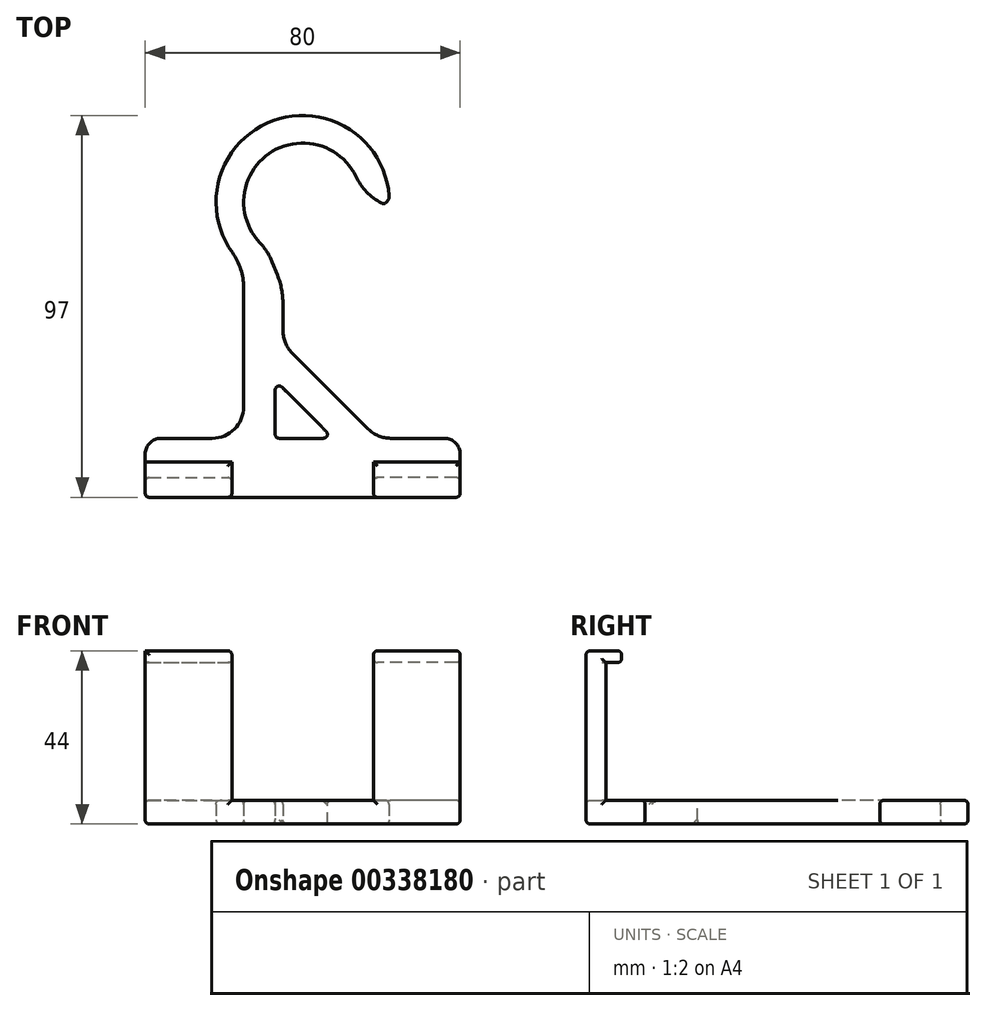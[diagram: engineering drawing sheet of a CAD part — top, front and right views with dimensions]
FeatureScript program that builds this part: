
annotation { "Feature Type Name" : "Feature", "Feature Type Description" : "" }
export const myFeature = defineFeature(function(context is Context, id is Id, definition is map)
    precondition{}
    {
        {
            var Q0;
            Q0=qCreatedBy(makeId("Top.planeOp"),FACE);
            var sketch = newSketch(context, id + "F0", { "sketchPlane" : qUnion([Q0])});
            skArc(sketch, "E0", {"start": v(13.52, 6.5) * mm, "mid": v(-8.54, 12.33) * mm, "end": v(-10.83, -10.37) * mm});
            skLineSegment(sketch, "E1.left", {"start": v(-15, -21.66) * mm, "end": v(-15, -52) * mm});
            skLineSegment(sketch, "E2", {"start": v(-23, -60) * mm, "end": v(-36, -60) * mm});
            skLineSegment(sketch, "E3", {"start": v(-40, -64) * mm, "end": v(-40, -75) * mm});
            skLineSegment(sketch, "E4", {"start": v(-40, -75) * mm, "end": v(40, -75) * mm});
            skLineSegment(sketch, "E5", {"start": v(40, -75) * mm, "end": v(40, -64) * mm});
            skLineSegment(sketch, "E6", {"start": v(36, -60) * mm, "end": v(22.31, -60) * mm});
            skLineSegment(sketch, "E7", {"start": v(-5, -25.91) * mm, "end": v(-5, -32.69) * mm});
            skLineSegment(sketch, "E8", {"start": v(-2.66, -38.34) * mm, "end": v(16.66, -57.66) * mm});
            skArc(sketch, "E9", {"start": v(21.94, 1.6) * mm, "mid": v(-7.53, 20.67) * mm, "end": v(-17.84, -12.88) * mm});
            skLineSegment(sketch, "E10", {"start": v(-7.72, -15.22) * mm, "end": v(-6.4, -18.54) * mm});
            skPoint(sketch, "E1.bottom.start.orphan", {"position": v(-15, 0) * mm});
            skLineSegment(sketch, "E11", {"start": v(-7, -45.31) * mm, "end": v(-7, -60) * mm});
            skLineSegment(sketch, "E12", {"start": v(-7, -60) * mm, "end": v(7.69, -60) * mm});
            skLineSegment(sketch, "E13", {"start": v(7.69, -60) * mm, "end": v(-7, -45.31) * mm});
            skPoint(sketch, "E14.visualSharp", {"position": v(-15, -16.1) * mm});
            skArc(sketch, "E14.filletArc", {"start": v(-15, -21.66) * mm, "mid": v(-15.73, -17.04) * mm, "end": v(-17.84, -12.88) * mm});
            skPoint(sketch, "E15.visualSharp", {"position": v(-5, -22.1) * mm});
            skArc(sketch, "E15.filletArc", {"start": v(-5, -25.91) * mm, "mid": v(-5.35, -22.16) * mm, "end": v(-6.4, -18.54) * mm});
            skPoint(sketch, "E16.visualSharp", {"position": v(-9, -12) * mm});
            skArc(sketch, "E16.filletArc", {"start": v(-7.72, -15.22) * mm, "mid": v(-9.04, -12.65) * mm, "end": v(-10.83, -10.37) * mm});
            skPoint(sketch, "E17.visualSharp", {"position": v(-5, -36) * mm});
            skArc(sketch, "E17.filletArc", {"start": v(-5, -32.69) * mm, "mid": v(-4.4, -35.75) * mm, "end": v(-2.66, -38.34) * mm});
            skPoint(sketch, "E18.visualSharp", {"position": v(19, -60) * mm});
            skArc(sketch, "E18.filletArc", {"start": v(16.66, -57.66) * mm, "mid": v(19.25, -59.4) * mm, "end": v(22.31, -60) * mm});
            skPoint(sketch, "E19.visualSharp", {"position": v(-15, -60) * mm});
            skArc(sketch, "E19.filletArc", {"start": v(-23, -60) * mm, "mid": v(-17.34, -57.66) * mm, "end": v(-15, -52) * mm});
            skPoint(sketch, "E20.visualSharp", {"position": v(40, -60) * mm});
            skArc(sketch, "E20.filletArc", {"start": v(40, -64) * mm, "mid": v(38.83, -61.17) * mm, "end": v(36, -60) * mm});
            skPoint(sketch, "E21.visualSharp", {"position": v(-40, -60) * mm});
            skArc(sketch, "E21.filletArc", {"start": v(-36, -60) * mm, "mid": v(-38.83, -61.17) * mm, "end": v(-40, -64) * mm});
            skPoint(sketch, "E22.visualSharp", {"position": v(22, 0) * mm});
            skArc(sketch, "E22.filletArc", {"start": v(18, 1) * mm, "mid": v(20.25, -0.52) * mm, "end": v(21.94, 1.6) * mm});
            skPoint(sketch, "E23.visualSharp", {"position": v(14.7, 3) * mm});
            skArc(sketch, "E23.filletArc", {"start": v(13.52, 6.5) * mm, "mid": v(16.4, 2.43) * mm, "end": v(20.45, -0.48) * mm});
            skSolve(sketch);
        }
        {
            var Q0;
            Q0 = qSketchRegion(id + "F0", true);
            extrude(context, id + "F1", {"entities" : qUnion([Q0]), "depth" : 6 * mm});
        }
        {
            var Q0;
            Q0=makeQuery(id+"F1.opExtrude","CAP_FACE",FACE,{"disambiguationData":[OSD([sQuery(id+"F0.wireOp",EDGE,"E0"),sQuery(id+"F0.wireOp",EDGE,"E1.left"),sQuery(id+"F0.wireOp",EDGE,"E2"),sQuery(id+"F0.wireOp",EDGE,"E3"),sQuery(id+"F0.wireOp",EDGE,"E4"),sQuery(id+"F0.wireOp",EDGE,"E5"),sQuery(id+"F0.wireOp",EDGE,"E6"),sQuery(id+"F0.wireOp",EDGE,"E7"),sQuery(id+"F0.wireOp",EDGE,"E8"),sQuery(id+"F0.wireOp",EDGE,"E9"),sQuery(id+"F0.wireOp",EDGE,"QrU3xHoO-jHLK-rufd-9GPx-dozL0sWFDDgJ"),sQuery(id+"F0.wireOp",EDGE,"E10"),sQuery(id+"F0.wireOp",EDGE,"E11"),sQuery(id+"F0.wireOp",EDGE,"E12"),sQuery(id+"F0.wireOp",EDGE,"E13")])],"isStart":false});
            var sketch = newSketch(context, id + "F2", { "sketchPlane" : qUnion([Q0])});
            skLineSegment(sketch, "E24.bottom", {"start": v(-40, -75) * mm, "end": v(-18, -75) * mm});
            skLineSegment(sketch, "E24.top", {"start": v(-40, -70) * mm, "end": v(-18, -70) * mm});
            skLineSegment(sketch, "E24.left", {"start": v(-40, -75) * mm, "end": v(-40, -70) * mm});
            skLineSegment(sketch, "E24.right", {"start": v(-18, -75) * mm, "end": v(-18, -70) * mm});
            skLineSegment(sketch, "E25.bottom", {"start": v(40, -75) * mm, "end": v(18, -75) * mm});
            skLineSegment(sketch, "E25.top", {"start": v(40, -70) * mm, "end": v(18, -70) * mm});
            skLineSegment(sketch, "E25.left", {"start": v(40, -75) * mm, "end": v(40, -70) * mm});
            skLineSegment(sketch, "E25.right", {"start": v(18, -75) * mm, "end": v(18, -70) * mm});
            skSolve(sketch);
        }
        {
            var Q0;
            Q0 = qSketchRegion(id + "F2", true);
            extrude(context, id + "F3", {"entities" : qUnion([Q0]), "operationType" : NewBodyOperationType.ADD, "depth" : 35 * mm});
        }
        {
            var Q0;
            Q0=makeQuery(id+"F3.opExtrude","CAP_FACE",FACE,{"disambiguationData":[OSD([sQuery(id+"F2.wireOp",EDGE,"E24.bottom"),sQuery(id+"F2.wireOp",EDGE,"E24.top"),sQuery(id+"F2.wireOp",EDGE,"E24.left"),sQuery(id+"F2.wireOp",EDGE,"E24.right")])],"isStart":false});
            var sketch = newSketch(context, id + "F4", { "sketchPlane" : qUnion([Q0])});
            skLineSegment(sketch, "E26.bottom", {"start": v(-40, -75) * mm, "end": v(-18, -75) * mm});
            skLineSegment(sketch, "E26.top", {"start": v(-40, -66) * mm, "end": v(-18, -66) * mm});
            skLineSegment(sketch, "E26.left", {"start": v(-40, -75) * mm, "end": v(-40, -66) * mm});
            skLineSegment(sketch, "E26.right", {"start": v(-18, -75) * mm, "end": v(-18, -66) * mm});
            skPoint(sketch, "E27.0", {"position": v(40, -75) * mm});
            skPoint(sketch, "E28.0", {"position": v(18, -70) * mm});
            skLineSegment(sketch, "E29.bottom", {"start": v(40, -75) * mm, "end": v(18, -75) * mm});
            skLineSegment(sketch, "E29.top", {"start": v(40, -66) * mm, "end": v(18, -66) * mm});
            skLineSegment(sketch, "E29.left", {"start": v(40, -75) * mm, "end": v(40, -66) * mm});
            skLineSegment(sketch, "E29.right", {"start": v(18, -75) * mm, "end": v(18, -66) * mm});
            skSolve(sketch);
        }
        {
            var Q0;
            Q0 = qSketchRegion(id + "F4", true);
            extrude(context, id + "F5", {"entities" : qUnion([Q0]), "operationType" : NewBodyOperationType.ADD, "depth" : 3 * mm});
        }
        {
            var Q0;
            Q0=makeQuery(id+"F1.opExtrude","SWEPT_EDGE",EDGE,{"disambiguationData":[OSD([sQuery(id+"F0.wireOp",EDGE,"E1.left"),sQuery(id+"F0.wireOp",EDGE,"E14.filletArc")])]});
            var Q1;
            Q1=makeQuery(id+"F1.opExtrude","SWEPT_EDGE",EDGE,{"disambiguationData":[OSD([sQuery(id+"F0.wireOp",EDGE,"E1.left"),sQuery(id+"F0.wireOp",EDGE,"E19.filletArc")])]});
            var Q2;
            Q2=makeQuery(id+"F1.opExtrude","SWEPT_EDGE",EDGE,{"disambiguationData":[OSD([sQuery(id+"F0.wireOp",EDGE,"E11"),sQuery(id+"F0.wireOp",EDGE,"E12")])]});
            var Q3;
            Q3=makeQuery(id+"F1.opExtrude","SWEPT_EDGE",EDGE,{"disambiguationData":[OSD([sQuery(id+"F0.wireOp",EDGE,"E6"),sQuery(id+"F0.wireOp",EDGE,"E20.filletArc")])]});
            var Q4;
            Q4=makeQuery(id+"F1.opExtrude","SWEPT_EDGE",EDGE,{"disambiguationData":[OSD([sQuery(id+"F0.wireOp",EDGE,"E6"),sQuery(id+"F0.wireOp",EDGE,"E18.filletArc")])]});
            var Q5;
            Q5=makeQuery(id+"F1.opExtrude","SWEPT_EDGE",EDGE,{"disambiguationData":[OSD([sQuery(id+"F0.wireOp",EDGE,"E8"),sQuery(id+"F0.wireOp",EDGE,"E17.filletArc")])]});
            var Q6;
            Q6=makeQuery(id+"F1.opExtrude","SWEPT_EDGE",EDGE,{"disambiguationData":[OSD([sQuery(id+"F0.wireOp",EDGE,"E8"),sQuery(id+"F0.wireOp",EDGE,"E18.filletArc")])]});
            var Q7;
            Q7=makeQuery(id+"F1.opExtrude","SWEPT_EDGE",EDGE,{"disambiguationData":[OSD([sQuery(id+"F0.wireOp",EDGE,"E5"),sQuery(id+"F0.wireOp",EDGE,"E20.filletArc")])]});
            var Q8;
            Q8=makeQuery(id+"F1.opExtrude","SWEPT_EDGE",EDGE,{"disambiguationData":[OSD([sQuery(id+"F0.wireOp",EDGE,"E6"),sQuery(id+"F0.wireOp",EDGE,"E20.filletArc")])]});
            var Q9;
            Q9=makeQuery(id+"F1.opExtrude","SWEPT_EDGE",EDGE,{"disambiguationData":[OSD([sQuery(id+"F0.wireOp",EDGE,"E6"),sQuery(id+"F0.wireOp",EDGE,"E18.filletArc")])]});
            var Q10;
            Q10=makeQuery(id+"F5.boolean.opBoolean","MERGE",EDGE,{"derivedFrom":[makeQuery(id+"F3.boolean.opBoolean","MERGE",EDGE,{"derivedFrom":[makeQuery(id+"F1.opExtrude","SWEPT_EDGE",EDGE,{"disambiguationData":[OSD([sQuery(id+"F0.wireOp",EDGE,"E4"),sQuery(id+"F0.wireOp",EDGE,"E5")])]}),makeQuery(id+"F3.opExtrude","SWEPT_EDGE",EDGE,{"disambiguationData":[OSD([sQuery(id+"F2.wireOp",EDGE,"E25.bottom"),sQuery(id+"F2.wireOp",EDGE,"E25.left")])]})]}),makeQuery(id+"F5.opExtrude","SWEPT_EDGE",EDGE,{"disambiguationData":[OSD([sQuery(id+"F4.wireOp",EDGE,"E29.bottom"),sQuery(id+"F4.wireOp",EDGE,"E29.left")])]})]});
            var Q11;
            Q11=makeQuery(id+"F1.opExtrude","SWEPT_EDGE",EDGE,{"disambiguationData":[OSD([sQuery(id+"F0.wireOp",EDGE,"E2"),sQuery(id+"F0.wireOp",EDGE,"E19.filletArc")])]});
            var Q12;
            Q12=makeQuery(id+"F1.opExtrude","SWEPT_EDGE",EDGE,{"disambiguationData":[OSD([sQuery(id+"F0.wireOp",EDGE,"E2"),sQuery(id+"F0.wireOp",EDGE,"E21.filletArc")])]});
            var Q13;
            Q13=makeQuery(id+"F1.opExtrude","SWEPT_EDGE",EDGE,{"disambiguationData":[OSD([sQuery(id+"F0.wireOp",EDGE,"E3"),sQuery(id+"F0.wireOp",EDGE,"E21.filletArc")])]});
            var Q14;
            Q14=makeQuery(id+"F5.boolean.opBoolean","MERGE",EDGE,{"derivedFrom":[makeQuery(id+"F3.boolean.opBoolean","MERGE",EDGE,{"derivedFrom":[makeQuery(id+"F1.opExtrude","SWEPT_EDGE",EDGE,{"disambiguationData":[OSD([sQuery(id+"F0.wireOp",EDGE,"E3"),sQuery(id+"F0.wireOp",EDGE,"E4")])]}),makeQuery(id+"F3.opExtrude","SWEPT_EDGE",EDGE,{"disambiguationData":[OSD([sQuery(id+"F2.wireOp",EDGE,"E24.bottom"),sQuery(id+"F2.wireOp",EDGE,"E24.left")])]})]}),makeQuery(id+"F5.opExtrude","SWEPT_EDGE",EDGE,{"disambiguationData":[OSD([sQuery(id+"F4.wireOp",EDGE,"E26.bottom"),sQuery(id+"F4.wireOp",EDGE,"E26.left")])]})]});
            var Q15;
            Q15=makeQuery(id+"F1.opExtrude","SWEPT_EDGE",EDGE,{"disambiguationData":[OSD([sQuery(id+"F0.wireOp",EDGE,"E1.left"),sQuery(id+"F0.wireOp",EDGE,"E14.filletArc")])]});
            var Q16;
            Q16=makeQuery(id+"F1.opExtrude","SWEPT_EDGE",EDGE,{"disambiguationData":[OSD([sQuery(id+"F0.wireOp",EDGE,"E1.left"),sQuery(id+"F0.wireOp",EDGE,"E19.filletArc")])]});
            var Q17;
            Q17=makeQuery(id+"F1.opExtrude","SWEPT_EDGE",EDGE,{"disambiguationData":[OSD([sQuery(id+"F0.wireOp",EDGE,"E2"),sQuery(id+"F0.wireOp",EDGE,"E19.filletArc")])]});
            var Q18;
            Q18=makeQuery(id+"F1.opExtrude","SWEPT_EDGE",EDGE,{"disambiguationData":[OSD([sQuery(id+"F0.wireOp",EDGE,"E2"),sQuery(id+"F0.wireOp",EDGE,"E21.filletArc")])]});
            var Q19;
            Q19=makeQuery(id+"F5.opExtrude","CAP_EDGE",EDGE,{"disambiguationData":[OSD([sQuery(id+"F4.wireOp",EDGE,"E26.bottom")])],"isStart":false});
            var Q20;
            Q20=makeQuery(id+"F5.opExtrude","CAP_EDGE",EDGE,{"disambiguationData":[OSD([sQuery(id+"F4.wireOp",EDGE,"E29.bottom")])],"isStart":false});
            var Q21;
            Q21=makeQuery(id+"F1.opExtrude","SWEPT_EDGE",EDGE,{"disambiguationData":[OSD([sQuery(id+"F0.wireOp",EDGE,"E0"),sQuery(id+"F0.wireOp",EDGE,"E23.filletArc")])]});
            var Q22;
            Q22=makeQuery(id+"F1.opExtrude","SWEPT_EDGE",EDGE,{"disambiguationData":[OSD([sQuery(id+"F0.wireOp",EDGE,"E0"),sQuery(id+"F0.wireOp",EDGE,"E16.filletArc")])]});
            var Q23;
            Q23=makeQuery(id+"F1.opExtrude","SWEPT_EDGE",EDGE,{"disambiguationData":[OSD([sQuery(id+"F0.wireOp",EDGE,"E0"),sQuery(id+"F0.wireOp",EDGE,"E23.filletArc")])]});
            var Q24;
            Q24=makeQuery(id+"F1.opExtrude","SWEPT_EDGE",EDGE,{"disambiguationData":[OSD([sQuery(id+"F0.wireOp",EDGE,"E0"),sQuery(id+"F0.wireOp",EDGE,"E16.filletArc")])]});
            var Q25;
            Q25=makeQuery(id+"F1.opExtrude","SWEPT_EDGE",EDGE,{"disambiguationData":[OSD([sQuery(id+"F0.wireOp",EDGE,"E10"),sQuery(id+"F0.wireOp",EDGE,"E16.filletArc")])]});
            var Q26;
            Q26=makeQuery(id+"F1.opExtrude","SWEPT_EDGE",EDGE,{"disambiguationData":[OSD([sQuery(id+"F0.wireOp",EDGE,"E10"),sQuery(id+"F0.wireOp",EDGE,"E15.filletArc")])]});
            var Q27;
            Q27=makeQuery(id+"F1.opExtrude","SWEPT_EDGE",EDGE,{"disambiguationData":[OSD([sQuery(id+"F0.wireOp",EDGE,"E7"),sQuery(id+"F0.wireOp",EDGE,"E15.filletArc")])]});
            var Q28;
            Q28=makeQuery(id+"F1.opExtrude","SWEPT_EDGE",EDGE,{"disambiguationData":[OSD([sQuery(id+"F0.wireOp",EDGE,"E7"),sQuery(id+"F0.wireOp",EDGE,"E17.filletArc")])]});
            var Q29;
            Q29=makeQuery(id+"F1.opExtrude","SWEPT_EDGE",EDGE,{"disambiguationData":[OSD([sQuery(id+"F0.wireOp",EDGE,"E10"),sQuery(id+"F0.wireOp",EDGE,"E16.filletArc")])]});
            var Q30;
            Q30=makeQuery(id+"F1.opExtrude","SWEPT_EDGE",EDGE,{"disambiguationData":[OSD([sQuery(id+"F0.wireOp",EDGE,"E10"),sQuery(id+"F0.wireOp",EDGE,"E15.filletArc")])]});
            var Q31;
            Q31=makeQuery(id+"F1.opExtrude","SWEPT_EDGE",EDGE,{"disambiguationData":[OSD([sQuery(id+"F0.wireOp",EDGE,"E7"),sQuery(id+"F0.wireOp",EDGE,"E15.filletArc")])]});
            var Q32;
            Q32=makeQuery(id+"F1.opExtrude","SWEPT_EDGE",EDGE,{"disambiguationData":[OSD([sQuery(id+"F0.wireOp",EDGE,"E7"),sQuery(id+"F0.wireOp",EDGE,"E17.filletArc")])]});
            var Q33;
            Q33=makeQuery(id+"F1.opExtrude","SWEPT_EDGE",EDGE,{"disambiguationData":[OSD([sQuery(id+"F0.wireOp",EDGE,"E8"),sQuery(id+"F0.wireOp",EDGE,"E17.filletArc")])]});
            var Q34;
            Q34=makeQuery(id+"F1.opExtrude","SWEPT_EDGE",EDGE,{"disambiguationData":[OSD([sQuery(id+"F0.wireOp",EDGE,"E8"),sQuery(id+"F0.wireOp",EDGE,"E18.filletArc")])]});
            var Q35;
            Q35=makeQuery(id+"F1.opExtrude","SWEPT_EDGE",EDGE,{"disambiguationData":[OSD([sQuery(id+"F0.wireOp",EDGE,"E11"),sQuery(id+"F0.wireOp",EDGE,"E13")])]});
            var Q36;
            Q36=makeQuery(id+"F1.opExtrude","SWEPT_EDGE",EDGE,{"disambiguationData":[OSD([sQuery(id+"F0.wireOp",EDGE,"E12"),sQuery(id+"F0.wireOp",EDGE,"E13")])]});
            var Q37;
            Q37=makeQuery(id+"F3.opExtrude","SWEPT_EDGE",EDGE,{"disambiguationData":[OSD([sQuery(id+"F0.wireOp",EDGE,"E3"),sQuery(id+"F2.wireOp",EDGE,"E24.top"),sQuery(id+"F2.wireOp",EDGE,"E24.left")])]});
            var Q38;
            Q38=makeQuery(id+"F3.opExtrude","SWEPT_EDGE",EDGE,{"disambiguationData":[OSD([sQuery(id+"F0.wireOp",EDGE,"E5"),sQuery(id+"F2.wireOp",EDGE,"E25.top"),sQuery(id+"F2.wireOp",EDGE,"E25.left")])]});
            var Q39;
            Q39=makeQuery(id+"F3.opExtrude","SWEPT_EDGE",EDGE,{"disambiguationData":[OSD([sQuery(id+"F2.wireOp",EDGE,"E25.top"),sQuery(id+"F2.wireOp",EDGE,"E25.right")])]});
            var Q40;
            Q40=makeQuery(id+"F3.opExtrude","SWEPT_EDGE",EDGE,{"disambiguationData":[OSD([sQuery(id+"F2.wireOp",EDGE,"E24.top"),sQuery(id+"F2.wireOp",EDGE,"E24.right")])]});
            var Q41;
            Q41=makeQuery(id+"F5.opExtrude","CAP_EDGE",EDGE,{"disambiguationData":[OSD([sQuery(id+"F4.wireOp",EDGE,"E26.top")])],"isStart":true});
            var Q42;
            Q42=makeQuery(id+"F5.opExtrude","CAP_EDGE",EDGE,{"disambiguationData":[OSD([sQuery(id+"F4.wireOp",EDGE,"E26.top")])],"isStart":false});
            var Q43;
            Q43=makeQuery(id+"F5.opExtrude","CAP_EDGE",EDGE,{"disambiguationData":[OSD([sQuery(id+"F4.wireOp",EDGE,"E29.top")])],"isStart":false});
            var Q44;
            Q44=makeQuery(id+"F5.opExtrude","CAP_EDGE",EDGE,{"disambiguationData":[OSD([sQuery(id+"F4.wireOp",EDGE,"E29.top")])],"isStart":true});
            var Q45;
            Q45=makeQuery(id+"F1.opExtrude","CAP_EDGE",EDGE,{"disambiguationData":[OSD([sQuery(id+"F0.wireOp",EDGE,"E2")])],"isStart":false});
            var Q46;
            Q46=makeQuery(id+"F1.opExtrude","CAP_EDGE",EDGE,{"disambiguationData":[OSD([sQuery(id+"F0.wireOp",EDGE,"E6")])],"isStart":false});
            var Q47;
            Q47=makeQuery(id+"F1.opExtrude","CAP_EDGE",EDGE,{"disambiguationData":[OSD([sQuery(id+"F0.wireOp",EDGE,"E3")])],"isStart":false});
            var Q48;
            Q48=makeQuery(id+"F1.opExtrude","CAP_EDGE",EDGE,{"disambiguationData":[OSD([sQuery(id+"F0.wireOp",EDGE,"E5")])],"isStart":false});
            var Q49;
            Q49=makeQuery(id+"F1.opExtrude","CAP_EDGE",EDGE,{"disambiguationData":[OSD([sQuery(id+"F0.wireOp",EDGE,"E5")])],"isStart":true});
            var Q50;
            Q50=makeQuery(id+"F5.opExtrude","CAP_EDGE",EDGE,{"disambiguationData":[OSD([sQuery(id+"F4.wireOp",EDGE,"E29.left")])],"isStart":false});
            var Q51;
            Q51=makeQuery(id+"F5.opExtrude","CAP_EDGE",EDGE,{"disambiguationData":[OSD([sQuery(id+"F4.wireOp",EDGE,"E29.left")])],"isStart":true});
            var Q52;
            Q52=makeQuery(id+"F5.opExtrude","CAP_EDGE",EDGE,{"disambiguationData":[OSD([sQuery(id+"F4.wireOp",EDGE,"E29.right")])],"isStart":true});
            var Q53;
            Q53=makeQuery(id+"F5.opExtrude","CAP_EDGE",EDGE,{"disambiguationData":[OSD([sQuery(id+"F4.wireOp",EDGE,"E29.right")])],"isStart":false});
            var Q54;
            Q54=makeQuery(id+"F5.boolean.opBoolean","MERGE",EDGE,{"derivedFrom":[makeQuery(id+"F3.opExtrude","SWEPT_EDGE",EDGE,{"disambiguationData":[OSD([sQuery(id+"F0.wireOp",EDGE,"E4"),sQuery(id+"F2.wireOp",EDGE,"E25.bottom"),sQuery(id+"F2.wireOp",EDGE,"E25.right")])]}),makeQuery(id+"F5.opExtrude","SWEPT_EDGE",EDGE,{"disambiguationData":[OSD([sQuery(id+"F4.wireOp",EDGE,"E29.bottom"),sQuery(id+"F4.wireOp",EDGE,"E29.right")])]})]});
            var Q55;
            Q55=makeQuery(id+"F1.opExtrude","CAP_EDGE",EDGE,{"disambiguationData":[OSD([sQuery(id+"F0.wireOp",EDGE,"E2")])],"isStart":true});
            var Q56;
            Q56=makeQuery(id+"F1.opExtrude","CAP_EDGE",EDGE,{"disambiguationData":[OSD([sQuery(id+"F0.wireOp",EDGE,"E3")])],"isStart":true});
            var Q57;
            Q57=makeQuery(id+"F1.opExtrude","CAP_EDGE",EDGE,{"disambiguationData":[OSD([sQuery(id+"F0.wireOp",EDGE,"E11")])],"isStart":true});
            var Q58;
            Q58=makeQuery(id+"F1.opExtrude","CAP_EDGE",EDGE,{"disambiguationData":[OSD([sQuery(id+"F0.wireOp",EDGE,"E8")])],"isStart":true});
            var Q59;
            Q59=makeQuery(id+"F1.opExtrude","CAP_EDGE",EDGE,{"disambiguationData":[OSD([sQuery(id+"F0.wireOp",EDGE,"E0")])],"isStart":true});
            var Q60;
            Q60=makeQuery(id+"F1.opExtrude","CAP_EDGE",EDGE,{"disambiguationData":[OSD([sQuery(id+"F0.wireOp",EDGE,"E0")])],"isStart":false});
            var Q61;
            Q61=makeQuery(id+"F1.opExtrude","CAP_EDGE",EDGE,{"disambiguationData":[OSD([sQuery(id+"F0.wireOp",EDGE,"E12")])],"isStart":false});
            var Q62;
            Q62=makeQuery(id+"F1.opExtrude","CAP_EDGE",EDGE,{"disambiguationData":[OSD([sQuery(id+"F0.wireOp",EDGE,"E4")])],"isStart":false});
            var Q63;
            Q63=makeQuery(id+"F5.boolean.opBoolean","MERGE",EDGE,{"derivedFrom":[makeQuery(id+"F3.opExtrude","SWEPT_EDGE",EDGE,{"disambiguationData":[OSD([sQuery(id+"F0.wireOp",EDGE,"E4"),sQuery(id+"F2.wireOp",EDGE,"E24.bottom"),sQuery(id+"F2.wireOp",EDGE,"E24.right")])]}),makeQuery(id+"F5.opExtrude","SWEPT_EDGE",EDGE,{"disambiguationData":[OSD([sQuery(id+"F4.wireOp",EDGE,"E26.bottom"),sQuery(id+"F4.wireOp",EDGE,"E26.right")])]})]});
            var Q64;
            Q64=makeQuery(id+"F5.boolean.opBoolean","MERGE",EDGE,{"derivedFrom":[makeQuery(id+"F3.boolean.opBoolean","MERGE",EDGE,{"derivedFrom":[makeQuery(id+"F1.opExtrude","SWEPT_EDGE",EDGE,{"disambiguationData":[OSD([sQuery(id+"F0.wireOp",EDGE,"E3"),sQuery(id+"F0.wireOp",EDGE,"E4")])]}),makeQuery(id+"F3.opExtrude","SWEPT_EDGE",EDGE,{"disambiguationData":[OSD([sQuery(id+"F2.wireOp",EDGE,"E24.bottom"),sQuery(id+"F2.wireOp",EDGE,"E24.left")])]})]}),makeQuery(id+"F5.opExtrude","SWEPT_EDGE",EDGE,{"disambiguationData":[OSD([sQuery(id+"F4.wireOp",EDGE,"E26.bottom"),sQuery(id+"F4.wireOp",EDGE,"E26.left")])]})]});
            var Q65;
            Q65=makeQuery(id+"F5.boolean.opBoolean","MERGE",FACE,{"derivedFrom":[makeQuery(id+"F3.boolean.opBoolean","MERGE",FACE,{"derivedFrom":[makeQuery(id+"F1.opExtrude","SWEPT_FACE",FACE,{"disambiguationData":[OSD([sQuery(id+"F0.wireOp",EDGE,"E4")])]}),makeQuery(id+"F3.opExtrude","SWEPT_FACE",FACE,{"disambiguationData":[OSD([sQuery(id+"F2.wireOp",EDGE,"E24.bottom")])]}),makeQuery(id+"F3.opExtrude","SWEPT_FACE",FACE,{"disambiguationData":[OSD([sQuery(id+"F2.wireOp",EDGE,"E25.bottom")])]})]}),makeQuery(id+"F5.opExtrude","SWEPT_FACE",FACE,{"disambiguationData":[OSD([sQuery(id+"F4.wireOp",EDGE,"E26.bottom")])]}),makeQuery(id+"F5.opExtrude","SWEPT_FACE",FACE,{"disambiguationData":[OSD([sQuery(id+"F4.wireOp",EDGE,"E29.bottom")])]})]});
            var Q66;
            Q66=makeQuery(id+"F5.opExtrude","CAP_EDGE",EDGE,{"disambiguationData":[OSD([sQuery(id+"F4.wireOp",EDGE,"E26.right")])],"isStart":false});
            var Q67;
            Q67=makeQuery(id+"F3.opExtrude","CAP_EDGE",EDGE,{"disambiguationData":[OSD([sQuery(id+"F2.wireOp",EDGE,"E24.top")])],"isStart":true});
            var Q68;
            Q68=makeQuery(id+"F3.opExtrude","CAP_EDGE",EDGE,{"disambiguationData":[OSD([sQuery(id+"F2.wireOp",EDGE,"E25.top")])],"isStart":true});
            var Q69;
            Q69=makeQuery(id+"F3.opExtrude","CAP_EDGE",EDGE,{"disambiguationData":[OSD([sQuery(id+"F2.wireOp",EDGE,"E25.top")])],"isStart":false});
            var Q70;
            Q70=makeQuery(id+"F3.opExtrude","CAP_EDGE",EDGE,{"disambiguationData":[OSD([sQuery(id+"F2.wireOp",EDGE,"E24.top")])],"isStart":false});
            var Q71;
            Q71=makeQuery(id+"F1.opExtrude","SWEPT_EDGE",EDGE,{"disambiguationData":[OSD([sQuery(id+"F0.wireOp",EDGE,"E22.filletArc"),sQuery(id+"F0.wireOp",EDGE,"E23.filletArc")]),ownerDisambiguation([makeQuery(id+"F0.imprint","IMPRINT",EDGE,{"derivedFrom":sQuery(id+"F0.wireOp",EDGE,"E0")})])]});
            fillet(context, id + "F6", {"entities" : qUnion([Q0, Q1, Q2, Q3, Q4, Q5, Q6, Q7, Q8, Q9, Q10, Q11, Q12, Q13, Q14, Q15, Q16, Q17, Q18, Q19, Q20, Q21, Q22, Q23, Q24, Q25, Q26, Q27, Q28, Q29, Q30, Q31, Q32, Q33, Q34, Q35, Q36, Q37, Q38, Q39, Q40, Q41, Q42, Q43, Q44, Q45, Q46, Q47, Q48, Q49, Q50, Q51, Q52, Q53, Q54, Q55, Q56, Q57, Q58, Q59, Q60, Q61, Q62, Q63, Q64, Q65, Q66, Q67, Q68, Q69, Q70, Q71]), "radius" : 1 * mm, "tangentPropagation" : true, "allowEdgeOverflow" : false});
        }
    });
